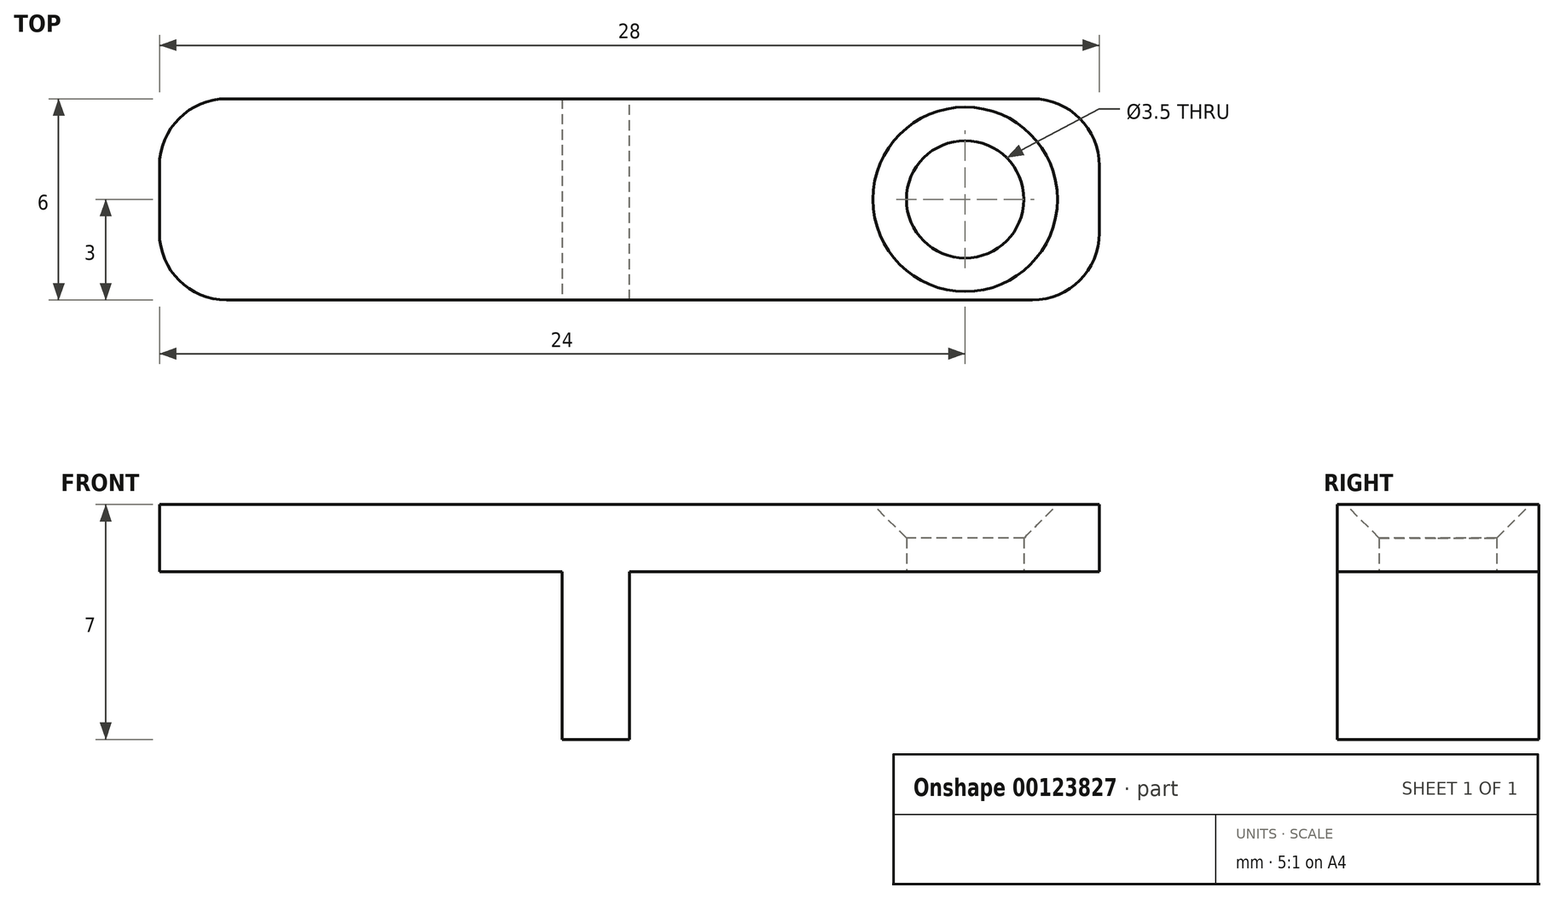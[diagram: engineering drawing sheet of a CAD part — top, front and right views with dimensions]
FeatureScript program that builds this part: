
annotation { "Feature Type Name" : "Feature", "Feature Type Description" : "" }
export const myFeature = defineFeature(function(context is Context, id is Id, definition is map)
    precondition{}
    {
        {
            var Q0;
            Q0=qCreatedBy(makeId("Top.planeOp"),FACE);
            var sketch = newSketch(context, id + "F0", { "sketchPlane" : qUnion([Q0])});
            skLineSegment(sketch, "E0.bottom", {"start": v(-14, 3) * mm, "end": v(14, 3) * mm});
            skLineSegment(sketch, "E0.top", {"start": v(-14, -3) * mm, "end": v(14, -3) * mm});
            skLineSegment(sketch, "E0.left", {"start": v(-14, 3) * mm, "end": v(-14, -3) * mm});
            skLineSegment(sketch, "E0.right", {"start": v(14, 3) * mm, "end": v(14, -3) * mm});
            skPoint(sketch, "E0.middle", {"position": v(0, 0) * mm});
            skPoint(sketch, "E1", {"position": v(10, 0) * mm});
            skLineSegment(sketch, "E2", {"start": v(0, 3) * mm, "end": v(0, -3) * mm, "construction": true});
            skCircle(sketch, "E3", {"center": v(10, 0) * mm, "radius": 1.75 * mm});
            skSolve(sketch);
        }
        {
            var Q0;
            Q0=makeQuery(id+"F0.imprint","IMPRINT",FACE,{"disambiguationData":[TD([[makeQuery(id+"F0.imprint","IMPRINT",EDGE,{"derivedFrom":sQuery(id+"F0.wireOp",EDGE,"E0.bottom")}),-1.0]])]});
            extrude(context, id + "F1", {"entities" : qUnion([Q0]), "depth" : 2 * mm});
        }
        {
            var Q0;
            Q0=makeQuery(id+"F1.opExtrude","CAP_FACE",FACE,{"disambiguationData":[OSD([sQuery(id+"F0.wireOp",EDGE,"E0.bottom"),sQuery(id+"F0.wireOp",EDGE,"E0.top"),sQuery(id+"F0.wireOp",EDGE,"E0.left"),sQuery(id+"F0.wireOp",EDGE,"E0.right"),sQuery(id+"F0.wireOp",EDGE,"E3")])],"isStart":true});
            var sketch = newSketch(context, id + "F2", { "sketchPlane" : qUnion([Q0])});
            skLineSegment(sketch, "E4", {"start": v(0, 3) * mm, "end": v(0, -3) * mm});
            skLineSegment(sketch, "E5", {"start": v(-2, -3) * mm, "end": v(-2, 3) * mm});
            skSolve(sketch);
        }
        {
            var Q0;
            {var subQ0=sQuery(id+"F2.wireOp",EDGE,"E4");Q0=makeQuery(id+"F2.imprint","IMPRINT",FACE,{"disambiguationData":[TD([[makeQuery(id+"F2.imprint","IMPRINT",EDGE,{"derivedFrom":subQ0}),-1.0]])]});}
            extrude(context, id + "F3", {"entities" : qUnion([Q0]), "operationType" : NewBodyOperationType.ADD, "depth" : 5 * mm});
        }
        {
            var Q0;
            Q0=makeQuery(id+"F1.opExtrude","CAP_EDGE",EDGE,{"disambiguationData":[OSD([sQuery(id+"F0.wireOp",EDGE,"E3")])],"isStart":false});
            chamfer(context, id + "F4", {"entities" : qUnion([Q0]), "width" : 1 * mm, "tangentPropagation" : true});
        }
        {
            var Q0;
            Q0=makeQuery(id+"F1.opExtrude","SWEPT_EDGE",EDGE,{"disambiguationData":[OSD([sQuery(id+"F0.wireOp",EDGE,"E0.top"),sQuery(id+"F0.wireOp",EDGE,"E0.right")])]});
            var Q1;
            Q1=makeQuery(id+"F1.opExtrude","SWEPT_EDGE",EDGE,{"disambiguationData":[OSD([sQuery(id+"F0.wireOp",EDGE,"E0.top"),sQuery(id+"F0.wireOp",EDGE,"E0.left")])]});
            var Q2;
            Q2=makeQuery(id+"F1.opExtrude","SWEPT_EDGE",EDGE,{"disambiguationData":[OSD([sQuery(id+"F0.wireOp",EDGE,"E0.bottom"),sQuery(id+"F0.wireOp",EDGE,"E0.left")])]});
            var Q3;
            Q3=makeQuery(id+"F1.opExtrude","SWEPT_EDGE",EDGE,{"disambiguationData":[OSD([sQuery(id+"F0.wireOp",EDGE,"E0.bottom"),sQuery(id+"F0.wireOp",EDGE,"E0.right")])]});
            fillet(context, id + "F5", {"entities" : qUnion([Q0, Q1, Q2, Q3]), "radius" : 2 * mm, "tangentPropagation" : true, "allowEdgeOverflow" : false});
        }
    });
